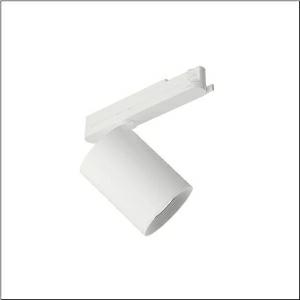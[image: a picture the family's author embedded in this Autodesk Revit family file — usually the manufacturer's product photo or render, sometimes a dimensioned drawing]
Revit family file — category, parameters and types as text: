
# Revit family: spot_21_51se13mbd5b
name_source: partatom
category: Lighting Fixtures
units: mm (PartAtom-declared; Revit-internal decimal feet)

## family parameters
Cut with Voids When Loaded = No
Host = Face
Light Source = No
Part Type = Normal
Room Calculation Point = No
Round Connector Dimension = Use Diameter
Shared = No

## types (1)
- --- (1 x LED, 5520 lm, 41.5 W, 4000K)
    Apparent Load = 42 VA
    CIE Flux Codes = 95 98 99 100 100
    Color Rendering = 90
    Color Temperature = 4000K
    Default Elevation = 1800 mm
    Description = Spot 21, directional spotlight, light control with lens, of PMMA, LED rated luminous flux: 5.300lm, light colour: 940, control gear: ECG Multilumen, with 3-phase adapter, mains connection: 220..240V, AC, 50/60Hz, of aluminium, traffic white (RAL 9016), length: 213mm, diameter: 105mm, protection rating (complete): IP20, insulation class (complete): insulation class I (protective earthing), certification: CE, impact resistance: IK02, permissible ambient temperature for indoor applications: -20..+40°C, packaging unit: 1 piece
    Height = 175 mm
    Lamp = 1 x LED
    Lamp Light Flux = 5520 lm
    Lamp Power = 41.5 W
    Lamp count = 1
    Length = 105 mm
    Luminous efficacy = 133 lm/W
    Manufacturer = Siteco
    ModVariant = No
    Model = 51SE13MBD5B
    Mounting Place = Ceiling
    Mounting Type = Pendant
    Number of Poles = 1
    OnlyDefault = Yes
    Power Factor = 1
    Product Name = Spot 21
    Product group = directional spotlight
    ProductGroupID = 904
    Protection Class = Protection class I
    Protection Degree = IP 20
    RLX_Detail_Level = 1
    RlxData = <blob elided: 17617 chars, md5=0994c8e7>
    Socket = socket
    Standby Power = 0 W
    System Light Flux = 5520 lm
    System Power = 42 W
    Type Comments = factory setting: luminous flux: 100 % | (ON | ON | ON | ON) | 1050 mA
    Type Image = l_1003976.jpg
    URL = http://relux.com
    VarID = @adj_053341
    Voltage = 0 V
    Weight = 0.00 kg
    Width = 0 mm  [stored 0 ft]

note: [stored X ft] marks values corroborated as IEEE doubles in the binary element streams (Revit-internal decimal feet)

## geometry (parser evidence)
native form markers: Blend x4, Sweep x9
no freeform markers — native parametric forms only
